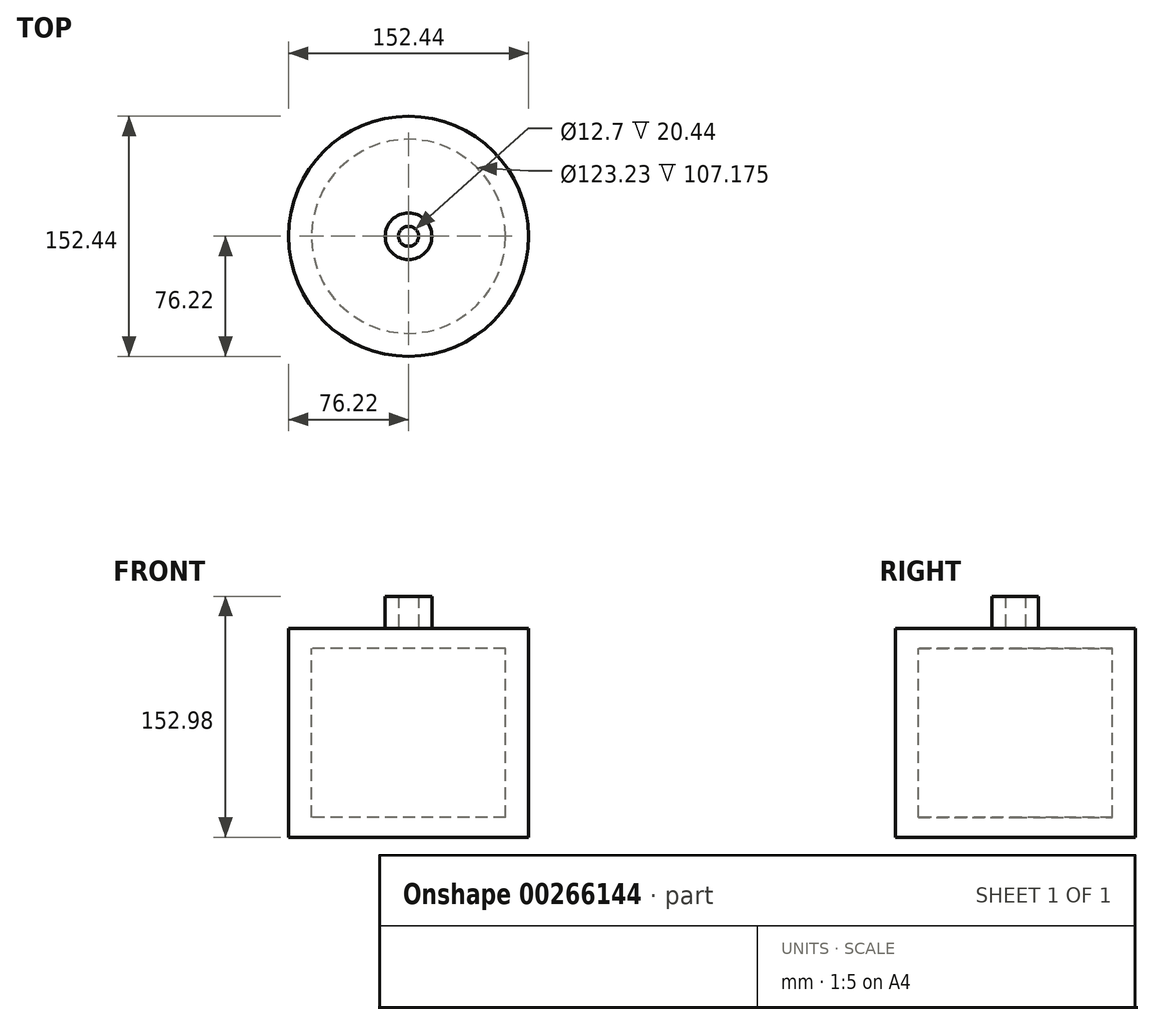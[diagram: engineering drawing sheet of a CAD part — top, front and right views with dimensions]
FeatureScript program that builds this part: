
annotation { "Feature Type Name" : "Feature", "Feature Type Description" : "" }
export const myFeature = defineFeature(function(context is Context, id is Id, definition is map)
    precondition{}
    {
        {
            var Q0;
            Q0=qCreatedBy(makeId("Front.planeOp"),FACE);
            var sketch = newSketch(context, id + "F0", { "sketchPlane" : qUnion([Q0])});
            skLineSegment(sketch, "E0", {"start": v(0, 76.49) * mm, "end": v(0, -76.49) * mm});
            skLineSegment(sketch, "E1", {"start": v(0, -76.49) * mm, "end": v(76.22, -76.49) * mm});
            skLineSegment(sketch, "E2", {"start": v(76.22, -76.49) * mm, "end": v(76.22, 56.05) * mm});
            skLineSegment(sketch, "E3", {"start": v(76.22, 56.05) * mm, "end": v(14.83, 56.05) * mm});
            skLineSegment(sketch, "E4", {"start": v(14.83, 56.05) * mm, "end": v(14.83, 76.48) * mm});
            skLineSegment(sketch, "E5", {"start": v(14.83, 76.48) * mm, "end": v(0, 76.49) * mm});
            skLineSegment(sketch, "E6", {"start": v(0, 43.32) * mm, "end": v(61.61, 43.32) * mm});
            skLineSegment(sketch, "E7", {"start": v(61.61, 43.32) * mm, "end": v(61.61, -63.86) * mm});
            skLineSegment(sketch, "E8", {"start": v(61.61, -63.86) * mm, "end": v(0, -63.86) * mm});
            skLineSegment(sketch, "E9", {"start": v(0, -63.86) * mm, "end": v(0, -76.49) * mm});
            skSolve(sketch);
        }
        {
            var Q0;
            Q0=makeQuery(id+"F0.imprint","IMPRINT",FACE,{"disambiguationData":[TD([[makeQuery(id+"F0.imprint","IMPRINT",EDGE,{"derivedFrom":sQuery(id+"F0.wireOp",EDGE,"E1")}),1.0]])]});
            var Q1;
            Q1=sQuery(id+"F0.wireOp",EDGE,"E0");
            revolve(context, id + "F1", {"entities" : qUnion([Q0]), "axis" : qUnion([Q1]), "revolveType" : RevolveType.FULL});
        }
        {
            var Q0;
            Q0=makeQuery(id+"F1.opRevolve","SWEPT_FACE",FACE,{"disambiguationData":[OSD([sQuery(id+"F0.wireOp",EDGE,"E3")])]});
            var sketch = newSketch(context, id + "F2", { "sketchPlane" : qUnion([Q0])});
            skCircle(sketch, "E10", {"center": v(0, 0) * mm, "radius": 8.11 * mm});
            skSolve(sketch);
        }
        {
            var Q0;
            Q0=sQuery(id+"F2.wireOp",VERTEX,"E10.center");
            var Q1;
            Q1=makeQuery(id+"F1.opRevolve","SWEPT_BODY",BODY,{"disambiguationData":[OSD([sQuery(id+"F0.wireOp",EDGE,"E0"),sQuery(id+"F0.wireOp",EDGE,"E1"),sQuery(id+"F0.wireOp",EDGE,"E2"),sQuery(id+"F0.wireOp",EDGE,"E3"),sQuery(id+"F0.wireOp",EDGE,"E4"),sQuery(id+"F0.wireOp",EDGE,"E5"),sQuery(id+"F0.wireOp",EDGE,"E6"),sQuery(id+"F0.wireOp",EDGE,"E7"),sQuery(id+"F0.wireOp",EDGE,"E8"),sQuery(id+"F0.wireOp",EDGE,"E9")])]});
            hole(context, id + "F3", {"style" : HoleStyle.SIMPLE, "endStyle" : HoleEndStyle.BLIND, "oppositeDirection" : true, "holeDiameter" : 12.7 * mm, "holeDepth" : 101.6 * mm, "tappedDepth" : 12.7 * mm, "tapClearance" : 3, "startFromSketch" : true, "locations" : qUnion([Q0]), "scope" : qUnion([Q1])});
        }
    });
